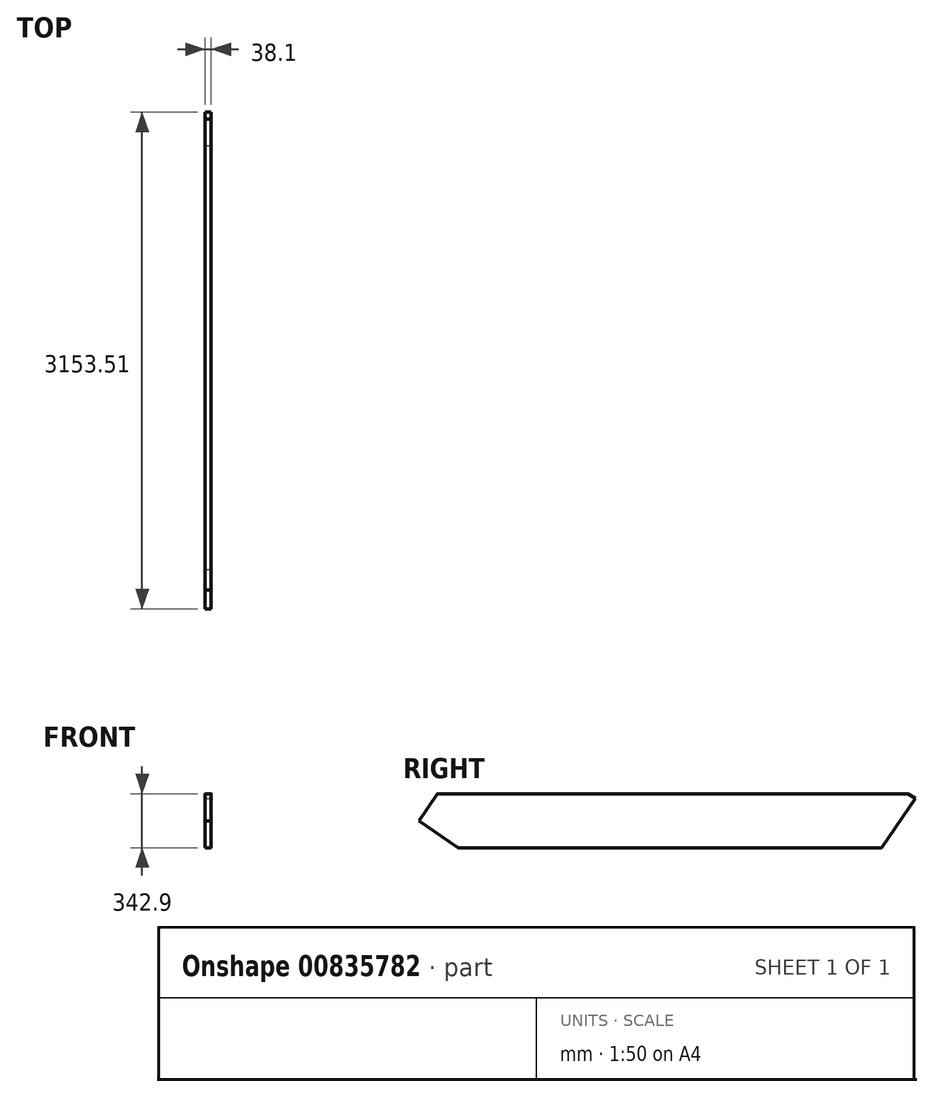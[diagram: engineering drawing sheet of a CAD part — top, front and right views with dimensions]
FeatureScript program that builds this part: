
annotation { "Feature Type Name" : "Feature", "Feature Type Description" : "" }
export const myFeature = defineFeature(function(context is Context, id is Id, definition is map)
    precondition{}
    {
        {
            var Q0;
            Q0=qCreatedBy(makeId("Front.planeOp"),FACE);
            var sketch = newSketch(context, id + "F0", { "sketchPlane" : qUnion([Q0])});
            skLineSegment(sketch, "E0.bottom", {"start": v(15.87, 171.45) * mm, "end": v(-15.88, 171.45) * mm});
            skLineSegment(sketch, "E0.top", {"start": v(15.88, -171.45) * mm, "end": v(-15.87, -171.45) * mm});
            skLineSegment(sketch, "E0.left", {"start": v(19.05, 168.28) * mm, "end": v(19.05, -168.28) * mm});
            skLineSegment(sketch, "E0.right", {"start": v(-19.05, 168.28) * mm, "end": v(-19.05, -168.28) * mm});
            skPoint(sketch, "E0.middle", {"position": v(0, 0) * mm});
            skPoint(sketch, "E1.visualSharp", {"position": v(-19.05, 171.45) * mm});
            skArc(sketch, "E1.filletArc", {"start": v(-15.88, 171.45) * mm, "mid": v(-18.12, 170.52) * mm, "end": v(-19.05, 168.28) * mm});
            skPoint(sketch, "E2.visualSharp", {"position": v(19.05, 171.45) * mm});
            skArc(sketch, "E2.filletArc", {"start": v(19.05, 168.28) * mm, "mid": v(18.12, 170.52) * mm, "end": v(15.87, 171.45) * mm});
            skPoint(sketch, "E3.visualSharp", {"position": v(19.05, -171.45) * mm});
            skArc(sketch, "E3.filletArc", {"start": v(15.88, -171.45) * mm, "mid": v(18.12, -170.52) * mm, "end": v(19.05, -168.28) * mm});
            skPoint(sketch, "E4.visualSharp", {"position": v(-19.05, -171.45) * mm});
            skArc(sketch, "E4.filletArc", {"start": v(-19.05, -168.28) * mm, "mid": v(-18.12, -170.52) * mm, "end": v(-15.87, -171.45) * mm});
            skSolve(sketch);
        }
        {
            var Q0;
            Q0 = qSketchRegion(id + "F0", true);
            extrude(context, id + "F1", {"entities" : qUnion([Q0]), "endBound" : BoundingType.SYMMETRIC, "depth" : 3657.6 * mm, "offsetDistance" : 25.4 * mm});
        }
        {
            var Q0;
            Q0=makeQuery(id+"F1.opExtrude","SWEPT_FACE",FACE,{"disambiguationData":[OSD([sQuery(id+"F0.wireOp",EDGE,"E0.left")])]});
            var sketch = newSketch(context, id + "F2", { "sketchPlane" : qUnion([Q0])});
            skLineSegment(sketch, "E5", {"start": v(-1465.02, 526.52) * mm, "end": v(-1828.8, 0) * mm});
            skLineSegment(sketch, "E6", {"start": v(-1828.8, 0) * mm, "end": v(-1580.65, -171.45) * mm});
            skLineSegment(sketch, "E7", {"start": v(-1580.65, -171.45) * mm, "end": v(-2148.9, -171.45) * mm});
            skLineSegment(sketch, "E8", {"start": v(-2148.9, -171.45) * mm, "end": v(-2148.9, 526.52) * mm});
            skLineSegment(sketch, "E9", {"start": v(-1465.02, 526.52) * mm, "end": v(-2148.9, 526.52) * mm});
            skSolve(sketch);
        }
        {
            var Q0;
            Q0 = qSketchRegion(id + "F2", true);
            extrude(context, id + "F3", {"entities" : qUnion([Q0]), "operationType" : NewBodyOperationType.REMOVE, "endBound" : BoundingType.THROUGH_ALL, "oppositeDirection" : true, "depth" : 25.4 * mm, "offsetDistance" : 25.4 * mm});
        }
        {
            var Q0;
            Q0=makeQuery(id+"F1.opExtrude","SWEPT_FACE",FACE,{"disambiguationData":[OSD([sQuery(id+"F0.wireOp",EDGE,"E0.left")])]});
            var sketch = newSketch(context, id + "F4", { "sketchPlane" : qUnion([Q0])});
            skLineSegment(sketch, "E10", {"start": v(1178.87, 241.3) * mm, "end": v(1324.7, 140.53) * mm});
            skLineSegment(sketch, "E11", {"start": v(1324.7, 140.53) * mm, "end": v(941.48, -414.13) * mm});
            skLineSegment(sketch, "E12", {"start": v(1178.87, 241.3) * mm, "end": v(1888.92, 241.3) * mm});
            skLineSegment(sketch, "E13", {"start": v(1888.92, 241.3) * mm, "end": v(1888.92, -414.13) * mm});
            skLineSegment(sketch, "E14", {"start": v(1888.92, -414.13) * mm, "end": v(941.48, -414.13) * mm});
            skPoint(sketch, "E15.orphan", {"position": v(1178.87, -414.13) * mm});
            skPoint(sketch, "E16.orphan", {"position": v(1528.11, 0) * mm});
            skSolve(sketch);
        }
        {
            var Q0;
            Q0 = qSketchRegion(id + "F4", true);
            extrude(context, id + "F5", {"entities" : qUnion([Q0]), "operationType" : NewBodyOperationType.REMOVE, "endBound" : BoundingType.THROUGH_ALL, "oppositeDirection" : true, "depth" : 25.4 * mm, "offsetDistance" : 25.4 * mm});
        }
    });
